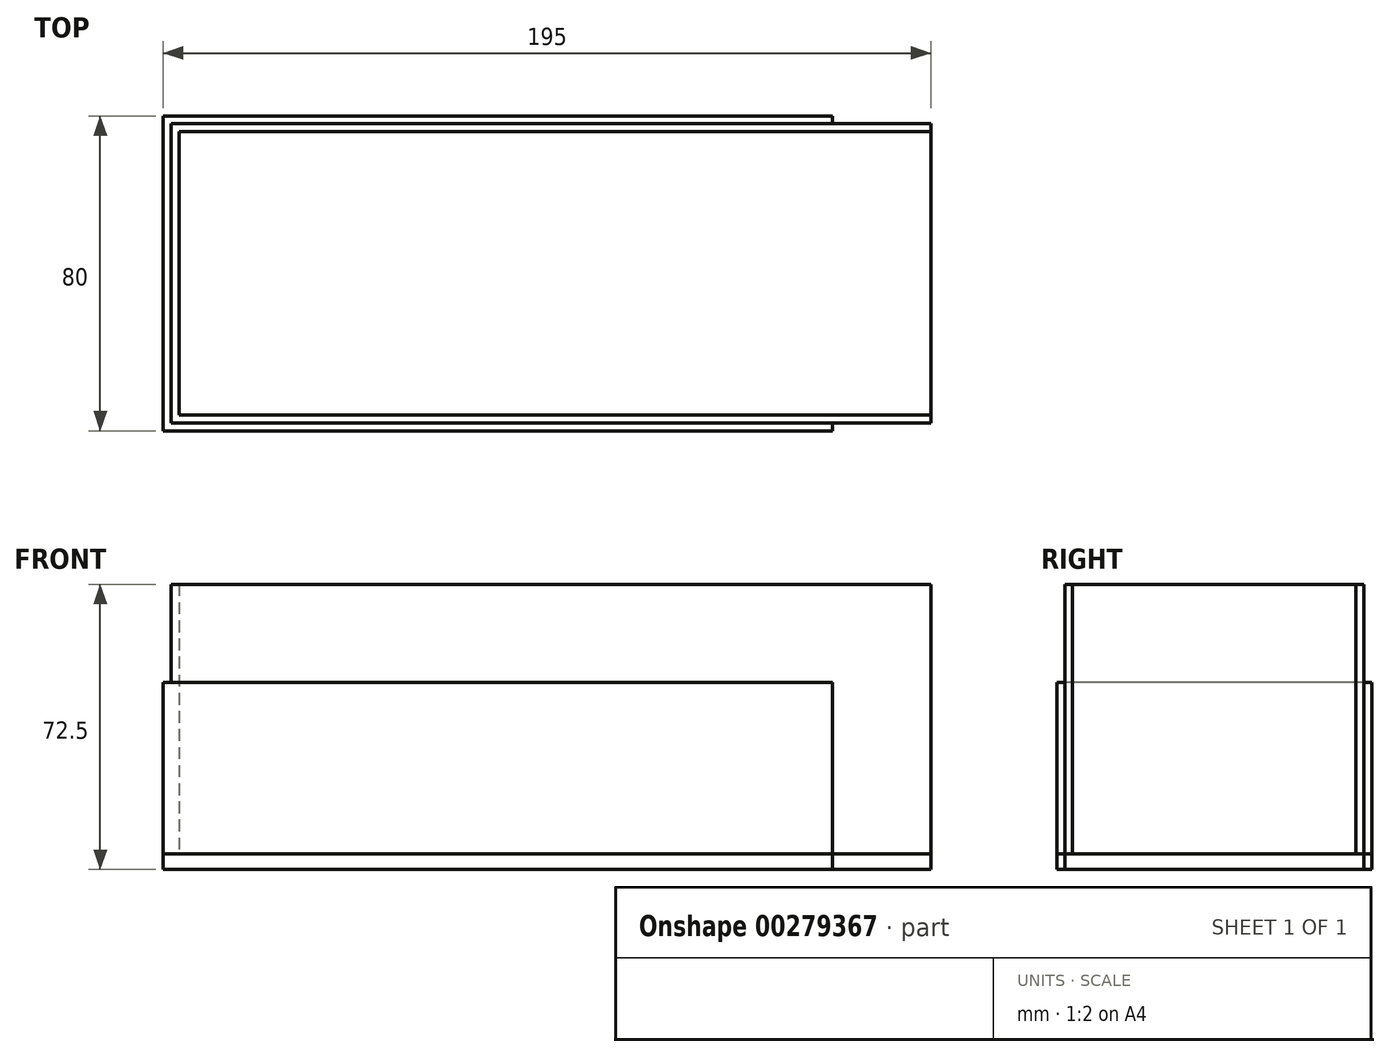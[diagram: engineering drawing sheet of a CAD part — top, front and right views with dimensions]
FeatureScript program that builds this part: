
annotation { "Feature Type Name" : "Feature", "Feature Type Description" : "" }
export const myFeature = defineFeature(function(context is Context, id is Id, definition is map)
    precondition{}
    {
        {
            var Q0;
            Q0=qCreatedBy(makeId("Top.planeOp"),FACE);
            var sketch = newSketch(context, id + "F0", { "sketchPlane" : qUnion([Q0])});
            skLineSegment(sketch, "E0", {"start": v(-189.63, 0) * mm, "end": v(207.94, 0) * mm, "construction": true});
            skLineSegment(sketch, "E1", {"start": v(0, 67.33) * mm, "end": v(0, 38) * mm, "construction": true});
            skLineSegment(sketch, "E2.0", {"start": v(-166, 36) * mm, "end": v(25, 36) * mm});
            skLineSegment(sketch, "E3.0", {"start": v(-166, 36) * mm, "end": v(-166, 0) * mm});
            skLineSegment(sketch, "E4.MirrorCS", {"start": v(-166, -36) * mm, "end": v(-166, 0) * mm});
            skLineSegment(sketch, "E5.MirrorCS", {"start": v(-166, -36) * mm, "end": v(25, -36) * mm});
            skLineSegment(sketch, "E6.0", {"start": v(-170, 40) * mm, "end": v(0, 40) * mm});
            skLineSegment(sketch, "E7.0", {"start": v(-170, 40) * mm, "end": v(-170, -40) * mm});
            skLineSegment(sketch, "E8.0", {"start": v(-170, -40) * mm, "end": v(0, -40) * mm});
            skLineSegment(sketch, "E9", {"start": v(0, 40) * mm, "end": v(0, 38) * mm});
            skLineSegment(sketch, "E10", {"start": v(0, -36) * mm, "end": v(0, -40) * mm});
            skLineSegment(sketch, "E11", {"start": v(0, 36) * mm, "end": v(0, -36) * mm});
            skLineSegment(sketch, "E12.0", {"start": v(25, 38) * mm, "end": v(25, 36) * mm});
            skLineSegment(sketch, "E13.0", {"start": v(0, 38) * mm, "end": v(25, 38) * mm});
            skLineSegment(sketch, "E14.trimOffspring", {"start": v(0, 36) * mm, "end": v(0, -76.99) * mm, "construction": true});
            skLineSegment(sketch, "E15.MirrorCS", {"start": v(0, -38) * mm, "end": v(25, -38) * mm});
            skLineSegment(sketch, "E16.MirrorCS", {"start": v(25, -38) * mm, "end": v(25, -36) * mm});
            skLineSegment(sketch, "E17", {"start": v(25, 36) * mm, "end": v(25, -36) * mm});
            skSolve(sketch);
        }
        {
            var Q0;
            {var subQ7=sQuery(id+"F0.wireOp",EDGE,"E3.0");Q0=makeQuery(id+"F0.imprint","IMPRINT",FACE,{"disambiguationData":[TD([[makeQuery(id+"F0.imprint","IMPRINT",EDGE,{"derivedFrom":subQ7}),-1.0]])]});}
            var Q1;
            {var subQ4=sQuery(id+"F0.wireOp",EDGE,"E15.MirrorCS");Q1=makeQuery(id+"F0.imprint","IMPRINT",FACE,{"disambiguationData":[TD([[makeQuery(id+"F0.imprint","IMPRINT",EDGE,{"derivedFrom":subQ4}),1.0]])]});}
            extrude(context, id + "F1", {"entities" : qUnion([Q0, Q1]), "depth" : 43.5 * mm, "offsetDistance" : 25 * mm});
        }
        {
            var Q0;
            {var subQ7=sQuery(id+"F0.wireOp",EDGE,"E3.0");Q0=makeQuery(id+"F0.imprint","IMPRINT",FACE,{"disambiguationData":[TD([[makeQuery(id+"F0.imprint","IMPRINT",EDGE,{"derivedFrom":subQ7}),-1.0]])]});}
            var Q1;
            {var subQ4=sQuery(id+"F0.wireOp",EDGE,"E15.MirrorCS");Q1=makeQuery(id+"F0.imprint","IMPRINT",FACE,{"disambiguationData":[TD([[makeQuery(id+"F0.imprint","IMPRINT",EDGE,{"derivedFrom":subQ4}),1.0]])]});}
            var Q2;
            {var subQ3=sQuery(id+"F0.wireOp",EDGE,"E3.0");Q2=makeQuery(id+"F0.imprint","IMPRINT",FACE,{"disambiguationData":[TD([[makeQuery(id+"F0.imprint","IMPRINT",EDGE,{"derivedFrom":subQ3}),1.0]])]});}
            var Q3;
            {var subQ2=sQuery(id+"F0.wireOp",EDGE,"E11");Q3=makeQuery(id+"F0.imprint","IMPRINT",FACE,{"disambiguationData":[TD([[makeQuery(id+"F0.imprint","IMPRINT",EDGE,{"derivedFrom":subQ2}),1.0]])]});}
            extrude(context, id + "F2", {"entities" : qUnion([Q0, Q1, Q2, Q3]), "oppositeDirection" : true, "depth" : 4 * mm, "offsetDistance" : 25 * mm});
        }
        {
            var Q0;
            Q0=makeQuery(id+"F1.opExtrude","CAP_FACE",FACE,{"disambiguationData":[OSD([sQuery(id+"F0.wireOp",EDGE,"E2.0"),sQuery(id+"F0.wireOp",EDGE,"E3.0"),sQuery(id+"F0.wireOp",EDGE,"E4.MirrorCS"),sQuery(id+"F0.wireOp",EDGE,"E5.MirrorCS"),sQuery(id+"F0.wireOp",EDGE,"E6.0"),sQuery(id+"F0.wireOp",EDGE,"E7.0"),sQuery(id+"F0.wireOp",EDGE,"E8.0"),sQuery(id+"F0.wireOp",EDGE,"E9"),sQuery(id+"F0.wireOp",EDGE,"E10"),sQuery(id+"F0.wireOp",EDGE,"E12.0"),sQuery(id+"F0.wireOp",EDGE,"E13.0"),sQuery(id+"F0.wireOp",EDGE,"E15.MirrorCS"),sQuery(id+"F0.wireOp",EDGE,"E16.MirrorCS")])],"isStart":false});
            var sketch = newSketch(context, id + "F3", { "sketchPlane" : qUnion([Q0])});
            skLineSegment(sketch, "E18.0", {"start": v(-166, 36) * mm, "end": v(25, 36) * mm});
            skLineSegment(sketch, "E19.0", {"start": v(-166, 36) * mm, "end": v(-166, 0) * mm});
            skLineSegment(sketch, "E20.0", {"start": v(-189.63, 0) * mm, "end": v(207.94, 0) * mm, "construction": true});
            skLineSegment(sketch, "E21.0", {"start": v(-168, 38) * mm, "end": v(25, 38) * mm});
            skLineSegment(sketch, "E22.0", {"start": v(-168, 38) * mm, "end": v(-168, 0) * mm});
            skLineSegment(sketch, "E23", {"start": v(-168, 0) * mm, "end": v(-166, 0) * mm});
            skLineSegment(sketch, "E24", {"start": v(25, 38) * mm, "end": v(25, 36) * mm});
            skLineSegment(sketch, "E25.MirrorCS", {"start": v(-168, -38) * mm, "end": v(25, -38) * mm});
            skLineSegment(sketch, "E26.MirrorCS", {"start": v(-166, -36) * mm, "end": v(25, -36) * mm});
            skLineSegment(sketch, "E27.MirrorCS", {"start": v(-168, -38) * mm, "end": v(-168, 0) * mm});
            skLineSegment(sketch, "E28.MirrorCS", {"start": v(-166, -36) * mm, "end": v(-166, 0) * mm});
            skLineSegment(sketch, "E29.MirrorCS", {"start": v(25, -38) * mm, "end": v(25, -36) * mm});
            skSolve(sketch);
        }
        {
            var Q0;
            Q0 = qSketchRegion(id + "F3", true);
            extrude(context, id + "F4", {"entities" : qUnion([Q0]), "operationType" : NewBodyOperationType.ADD, "depth" : 25 * mm, "offsetDistance" : 25 * mm});
        }
    });
